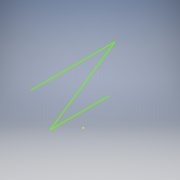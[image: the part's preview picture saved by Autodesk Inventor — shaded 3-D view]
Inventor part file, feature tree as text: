
AUTODESK INVENTOR PART (.ipt)
format: ipt  version: 2018 (Build 220112000, 112)  size: 83,456 bytes
history: native  units: in
note: dims shown in document units (in); Inventor stores cm internally (conversion verified against a paired STEP export)
features: sketch x1
ambient origin geometry x8: Origin, YZ Plane, XZ Plane, XY Plane, X Axis, Y Axis, Z Axis, Center Point
feature tree (1):
  sketch  "Sketch1"
